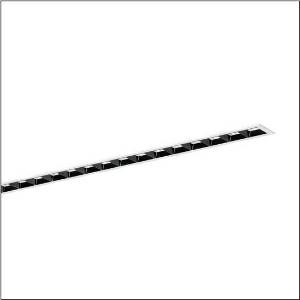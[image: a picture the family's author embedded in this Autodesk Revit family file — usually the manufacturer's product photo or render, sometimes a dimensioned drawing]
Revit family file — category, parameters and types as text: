
# Revit family: silica_21_51mx11tctaw
name_source: partatom
category: Lighting Fixtures
units: mm (PartAtom-declared; Revit-internal decimal feet)

## family parameters
Cut with Voids When Loaded = No
Host = Face
Light Source = No
Part Type = Normal
Room Calculation Point = No
Round Connector Dimension = Use Diameter
Shared = No

## types (1)
- --- (1 x LED, 9300 lm, 80.5 W, 6500K)
    Apparent Load = 81 VA
    CIE Flux Codes = 85 99 100 100 100
    Color Rendering = 80
    Color Temperature = 6500K
    Default Elevation = 1800 mm
    Description = Silica 21, office luminaire, primary light control with darklight reflector, of PMMA, black, CAT 2 (L<= 3000cd/m²), light emission: direct distribution, primary light characteristic: symmetric, installation type: recessed, LED, rated luminous flux: 9.300lm, luminous efficacy: 110lm/W, light colour: 8tw, colour temperature: 2700..6500K, control gear: DALI DT8, with terminal, 3+2-pole, max. 2.5mm², mains connection: 220..240V, AC, 50/60Hz, rated input power: 84.6W, luminaire housing, of aluminium, traffic white (RAL 9016), length: 3.028mm, width: 79mm, height: 53mm, protection rating (complete): IP20, insulation class (complete): insulation class I (protective earthing), certification: CE, ENEC, VDE, permissible operating ambient temperature: 0..+35°C, standard: EN 50419, packaging unit: 1 piece
    Height = 0 mm  [stored 0 ft]
    Lamp = 1 x LED
    Lamp Light Flux = 9300 lm
    Lamp Power = 80.5 W
    Lamp count = 1
    Length = 3027 mm
    Luminous efficacy = 116 lm/W
    Manufacturer = Siteco
    ModVariant = No
    Model = 51MX11TCTAW
    Mounting Place = Ceiling
    Mounting Type = Recessed
    Number of Poles = 1
    OnlyDefault = Yes
    Power Factor = 1
    Product Name = Silica 21
    Product group = office luminaire | ceiling recessed
    ProductGroupID = 400
    Protection Class = Protection class I
    Protection Degree = IP 20
    RLX_Detail_Level = 1
    RLX_Emergency_Light_Flux = 0 lm
    RLX_Emergency_Type = 0
    RLX_Emergency_Type_DB = No
    RlxData = <blob elided: 59609 chars, md5=23b99c2a>
    Socket = socket
    Standby Power = 0 W
    System Light Flux = 9300 lm
    System Power = 81 W
    Type Comments = individual setting
    Type Image = l_1335880.jpg
    URL = http://relux.com
    VarID = @adj_139589
    Voltage = 0 V
    Weight = 0.00 kg
    Width = 79 mm

note: [stored X ft] marks values corroborated as IEEE doubles in the binary element streams (Revit-internal decimal feet)

## geometry (parser evidence)
native form markers: Blend x4, Sweep x10
no freeform markers — native parametric forms only
